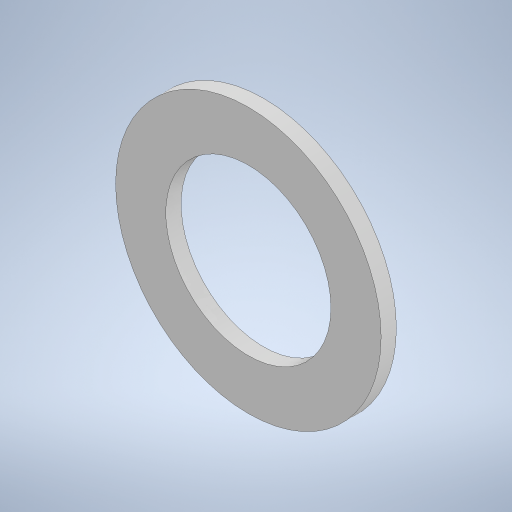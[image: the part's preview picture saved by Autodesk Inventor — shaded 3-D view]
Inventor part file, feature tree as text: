
AUTODESK INVENTOR PART (.ipt)
format: ipt  version: 2023 (Build 270158000, 158)  size: 226,816 bytes
history: native  units: in
note: dims shown in document units (in); Inventor stores cm internally (conversion verified against a paired STEP export)
features: extrude x1, sketch x1
ambient origin geometry x8: Origin, YZ Plane, XZ Plane, XY Plane, X Axis, Y Axis, Z Axis, Center Point
bodies: Solid1 (feature_tree)
feature tree (2):
  extrude  "Extrusion1"  Depth=0.0236in
  sketch  "Sketch1"  dims[d0=0.4114in d1=0.2559in d2=0.0236in d3=0.0in]
